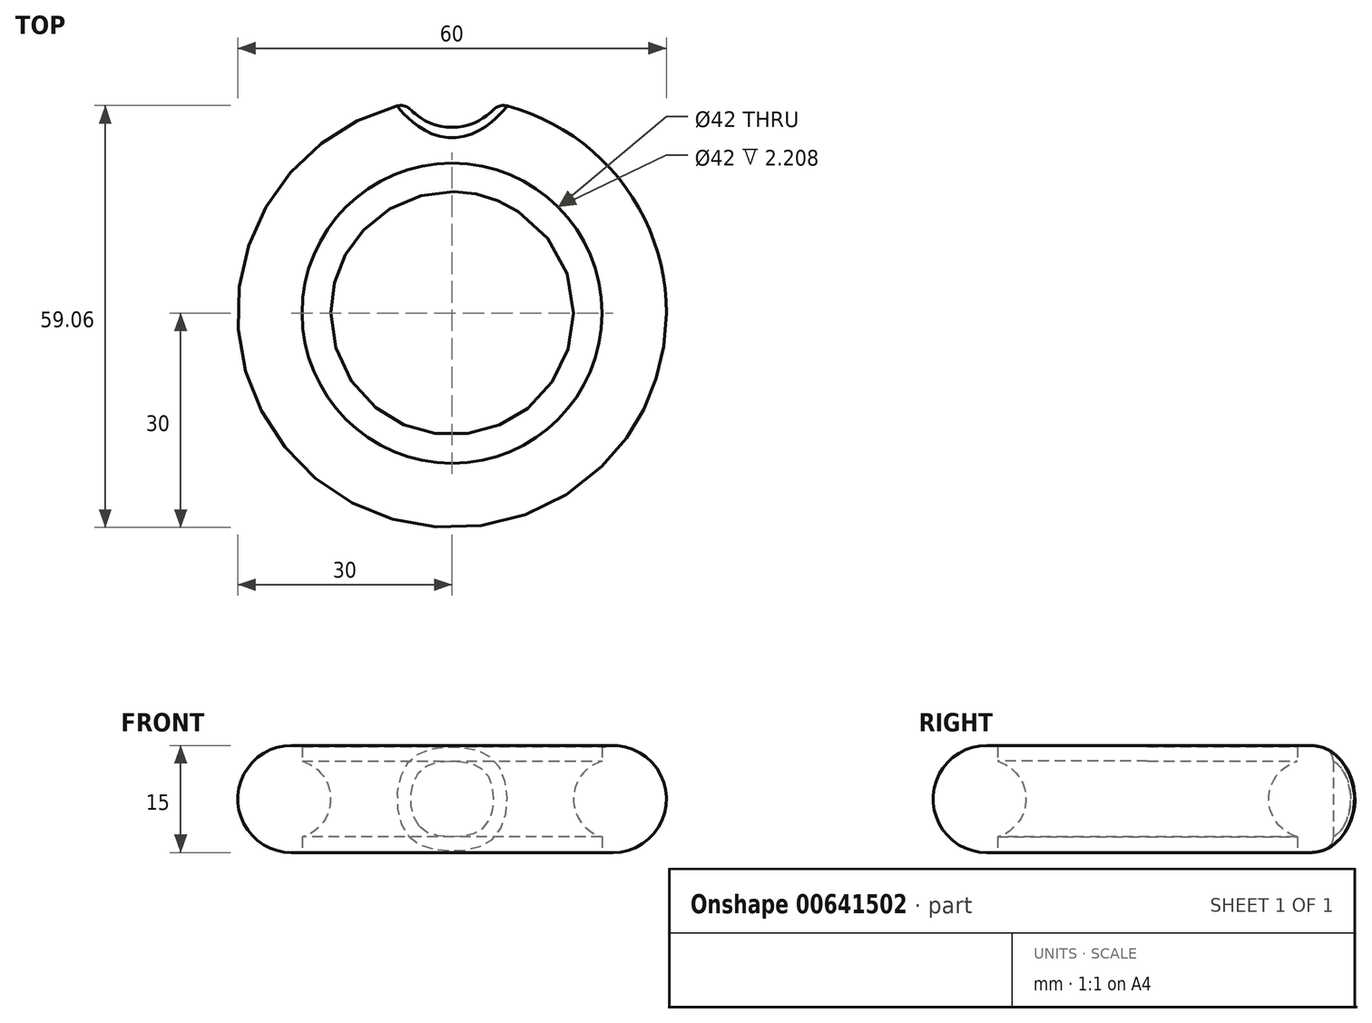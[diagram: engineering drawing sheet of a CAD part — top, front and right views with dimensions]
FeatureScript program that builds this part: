
annotation { "Feature Type Name" : "Feature", "Feature Type Description" : "" }
export const myFeature = defineFeature(function(context is Context, id is Id, definition is map)
    precondition{}
    {
        {
            var Q0;
            Q0=qCreatedBy(makeId("Front.planeOp"),FACE);
            var sketch = newSketch(context, id + "F0", { "sketchPlane" : qUnion([Q0])});
            skArc(sketch, "E0", {"start": v(-19.32, 14.3) * mm, "mid": v(-29.82, 9.13) * mm, "end": v(-22.5, 0) * mm});
            skArc(sketch, "E1", {"start": v(-19.32, 14.3) * mm, "mid": v(-9.9, 11.09) * mm, "end": v(0, 10) * mm});
            skLineSegment(sketch, "E2", {"start": v(0, 0) * mm, "end": v(-22.5, 0) * mm});
            skLineSegment(sketch, "E3.trimOffspring", {"start": v(0, 10) * mm, "end": v(0, 0) * mm});
            skSolve(sketch);
        }
        {
            var Q0;
            Q0 = qSketchRegion(id + "F0", true);
            var Q1;
            Q1=sQuery(id+"F0.wireOp",EDGE,"E3.trimOffspring");
            revolve(context, id + "F1", {"entities" : qUnion([Q0]), "axis" : qUnion([Q1]), "revolveType" : RevolveType.FULL});
        }
        {
            var Q0;
            Q0=qCreatedBy(makeId("Top.planeOp"),FACE);
            var sketch = newSketch(context, id + "F2", { "sketchPlane" : qUnion([Q0])});
            skCircle(sketch, "E4", {"center": v(0, 0) * mm, "radius": 21 * mm});
            skSolve(sketch);
        }
        {
            var Q0;
            Q0 = qSketchRegion(id + "F2", true);
            extrude(context, id + "F3", {"entities" : qUnion([Q0]), "operationType" : NewBodyOperationType.REMOVE, "depth" : 25 * mm, "offsetDistance" : 25 * mm});
        }
        {
            var Q0;
            Q0=qCreatedBy(makeId("Front.planeOp"),FACE);
            var sketch = newSketch(context, id + "F4", { "sketchPlane" : qUnion([Q0])});
            skCircle(sketch, "E5", {"center": v(-22.5, 7.5) * mm, "radius": 5.5 * mm});
            skSolve(sketch);
        }
        {
            var Q0;
            Q0 = qSketchRegion(id + "F4", true);
            var Q1;
            Q1=sQuery(id+"F0.wireOp",EDGE,"E3.trimOffspring");
            revolve(context, id + "F5", {"operationType" : NewBodyOperationType.ADD, "entities" : qUnion([Q0]), "axis" : qUnion([Q1]), "revolveType" : RevolveType.FULL});
        }
        {
            var Q0;
            Q0=qCreatedBy(makeId("Top.planeOp"),FACE);
            var sketch = newSketch(context, id + "F6", { "sketchPlane" : qUnion([Q0])});
            skCircle(sketch, "E6", {"center": v(0, 34) * mm, "radius": 8 * mm});
            skSolve(sketch);
        }
        {
            var Q0;
            Q0 = qSketchRegion(id + "F6", true);
            extrude(context, id + "F7", {"entities" : qUnion([Q0]), "operationType" : NewBodyOperationType.REMOVE, "depth" : 25 * mm, "offsetDistance" : 25 * mm});
        }
        {
            var Q0;
            Q0=makeQuery(id+"F7.boolean.opBoolean","INTERSECT",EDGE,{"derivedFrom":[makeQuery(id+"F1.opRevolve","SWEPT_FACE",FACE,{"disambiguationData":[OSD([sQuery(id+"F0.wireOp",EDGE,"E0")])]}),makeQuery(id+"F7.opExtrude","SWEPT_FACE",FACE,{"disambiguationData":[OSD([sQuery(id+"F6.wireOp",EDGE,"E6")])]})]});
            fillet(context, id + "F8", {"entities" : qUnion([Q0]), "radius" : 2 * mm, "tangentPropagation" : true, "allowEdgeOverflow" : false});
        }
    });
